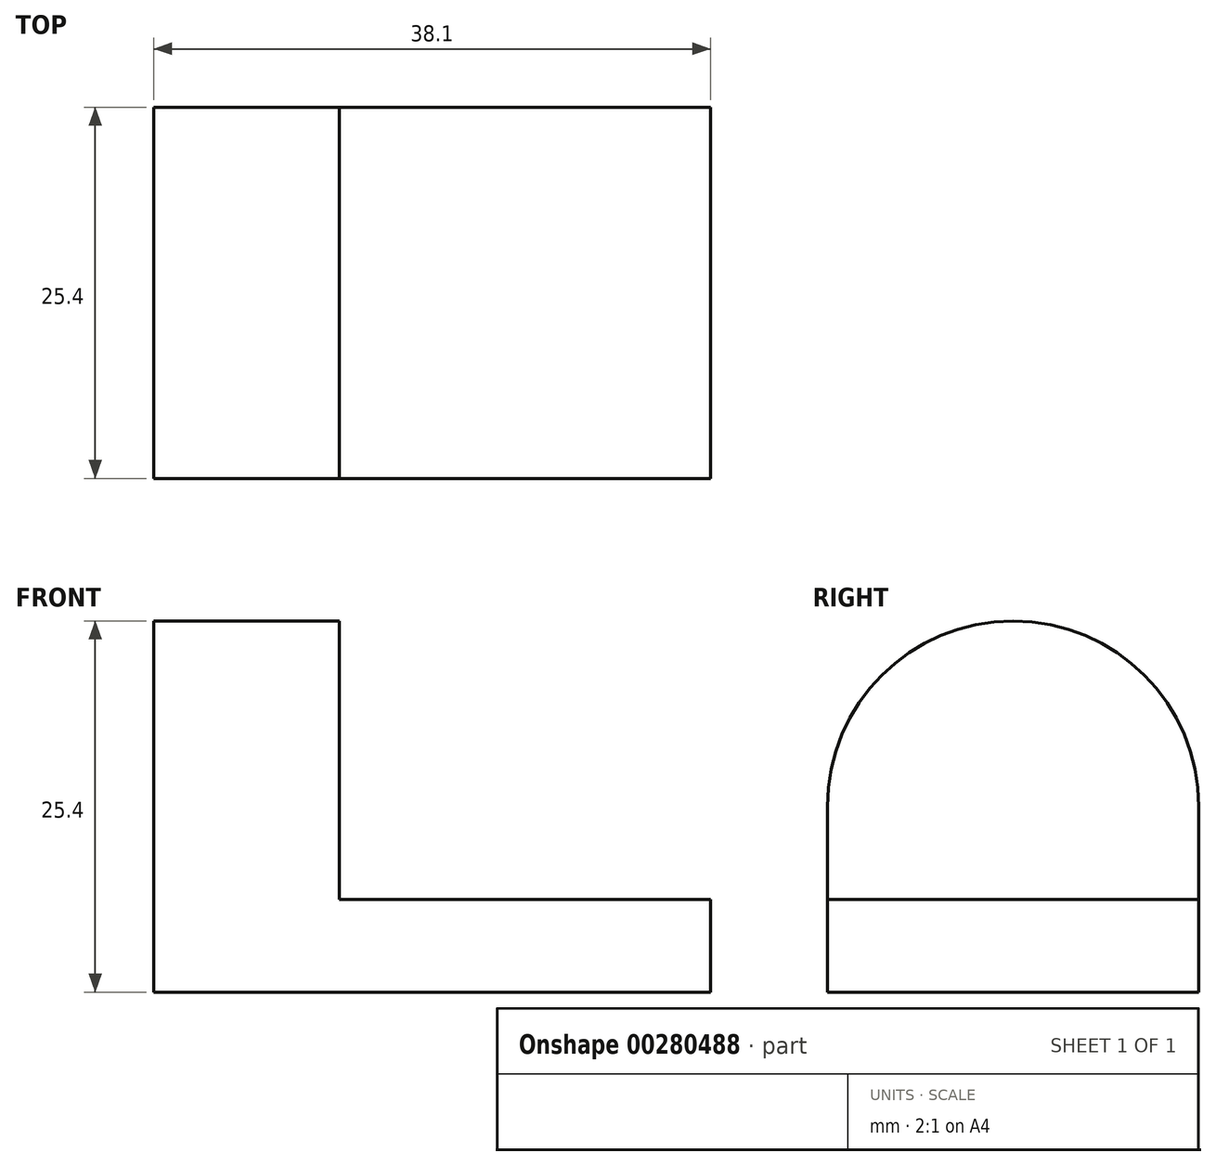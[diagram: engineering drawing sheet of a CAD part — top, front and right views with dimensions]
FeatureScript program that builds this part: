
annotation { "Feature Type Name" : "Feature", "Feature Type Description" : "" }
export const myFeature = defineFeature(function(context is Context, id is Id, definition is map)
    precondition{}
    {
        {
            var Q0;
            Q0=qCreatedBy(makeId("Front.planeOp"),FACE);
            var sketch = newSketch(context, id + "F0", { "sketchPlane" : qUnion([Q0])});
            skLineSegment(sketch, "E0", {"start": v(0, 0) * mm, "end": v(0, 25.4) * mm});
            skLineSegment(sketch, "E1", {"start": v(0, 25.4) * mm, "end": v(12.7, 25.4) * mm});
            skLineSegment(sketch, "E2", {"start": v(12.7, 25.4) * mm, "end": v(12.7, 6.35) * mm});
            skLineSegment(sketch, "E3", {"start": v(0, 0) * mm, "end": v(38.1, 0) * mm});
            skLineSegment(sketch, "E4", {"start": v(38.1, 6.35) * mm, "end": v(12.7, 6.35) * mm});
            skLineSegment(sketch, "E5", {"start": v(38.1, 6.35) * mm, "end": v(38.1, 0) * mm});
            skSolve(sketch);
        }
        {
            var Q0;
            Q0 = qSketchRegion(id + "F0", true);
            extrude(context, id + "F1", {"entities" : qUnion([Q0]), "depth" : 25.4 * mm});
        }
        {
            var Q0;
            Q0=makeQuery(id+"F1.opExtrude","SWEPT_FACE",FACE,{"disambiguationData":[OSD([sQuery(id+"F0.wireOp",EDGE,"E1")])]});
            var sketch = newSketch(context, id + "F2", { "sketchPlane" : qUnion([Q0])});
            skLineSegment(sketch, "E6.bottom", {"start": v(0, 0) * mm, "end": v(12.7, 0) * mm});
            skLineSegment(sketch, "E6.top", {"start": v(0, -25.4) * mm, "end": v(12.7, -25.4) * mm});
            skLineSegment(sketch, "E6.left", {"start": v(0, 0) * mm, "end": v(0, -25.4) * mm});
            skLineSegment(sketch, "E6.right", {"start": v(12.7, 0) * mm, "end": v(12.7, -25.4) * mm});
            skSolve(sketch);
        }
        {
            var Q0;
            Q0 = qSketchRegion(id + "F2", true);
            extrude(context, id + "F3", {"entities" : qUnion([Q0]), "operationType" : NewBodyOperationType.REMOVE, "oppositeDirection" : true, "depth" : 12.7 * mm});
        }
        {
            var Q0;
            Q0=qCreatedBy(makeId("Right.planeOp"),FACE);
            var sketch = newSketch(context, id + "F4", { "sketchPlane" : qUnion([Q0])});
            skArc(sketch, "E7", {"start": v(0, 12.7) * mm, "mid": v(-12.7, 25.4) * mm, "end": v(-25.4, 12.7) * mm});
            skLineSegment(sketch, "E8", {"start": v(-25.4, 12.7) * mm, "end": v(0, 12.7) * mm});
            skSolve(sketch);
        }
        {
            var Q0;
            Q0 = qSketchRegion(id + "F4", true);
            extrude(context, id + "F5", {"entities" : qUnion([Q0]), "operationType" : NewBodyOperationType.ADD, "depth" : 12.7 * mm});
        }
    });
